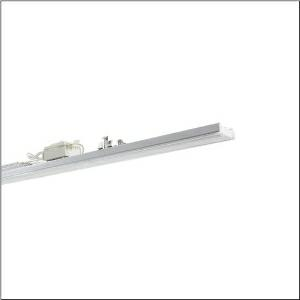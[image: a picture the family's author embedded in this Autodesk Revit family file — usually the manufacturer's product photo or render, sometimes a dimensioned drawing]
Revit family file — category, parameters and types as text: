
# Revit family: licross_r__11_recessed_ho_51te1edv4m5s_c22c
name_source: partatom
category: Lighting Fixtures
units: mm (PartAtom-declared; Revit-internal decimal feet)

## family parameters
Cut with Voids When Loaded = No
Host = Face
Light Source = No
Part Type = Normal
Room Calculation Point = No
Round Connector Dimension = Use Diameter
Shared = No

## types (1)
- --- (1 x LED, 25560 lm, 144.7 W, 4000K)
    Apparent Load = 145 VA
    CIE Flux Codes = 85 95 99 100 100
    Color Rendering = 80
    Color Temperature = 4000K
    Default Elevation = 1800 mm
    Description = Licross® 11 Recessed HO, luminaire insert, of sheet steel, galvanised, coil coated, white, length: 2.250mm, width: 66mm, height: 67mm, LED rated luminous flux: 25.560lm, light colour: 840, control gear: DALI 2, with plug, 5-pole, with phase selection, mains connection: 220..240V, AC, 50/60Hz, rated input power: 145W, internal wiring halogen-free, primary light control with lens, of plastic, primary optical cover: cover, of PMMA, light emission: direct distribution, primary light characteristic: symmetric, protection rating (complete): IP54, insulation class (complete): insulation class I (protective earthing), certification: CE, ENEC, VDE, UKCA, protection symbol: D if used in an environment with non-conductive dust loads with corresponding accessories, impact resistance: IK06, permissible ambient temperature for indoor applications: -40..+35°C, corresponds to IFS (International Featured Standards) requirements for safety and quality in the food industry, reducing of maximum allowable ambient temperature of 5°C with ceiling mounting, LABS conformity tested according to VDMA 24364:2018-05, packaging unit: 1 piece
    Height = 58 mm
    Lamp = 1 x LED
    Lamp Light Flux = 25560 lm
    Lamp Power = 144.7 W
    Lamp count = 1
    Length = 2250 mm
    Luminous efficacy = 177 lm/W
    Manufacturer = Siteco
    ModVariant = No
    Model = 51TE1EDV4M5S
    Mounting Place = Ceiling
    Mounting Type = Pendant
    Number of Poles = 1
    OnlyDefault = Yes
    Power Factor = 1
    Product Name = Licross® 11 Recessed HO
    Product group = luminaire insert | ceiling pendant
    ProductGroupID = 902
    Protection Class = Protection class I
    Protection Degree = IP 54
    RLX_Detail_Level = 1
    RLX_Emergency_Light_Flux = 0 lm
    RLX_Emergency_Type = 0
    RLX_Emergency_Type_DB = No
    RlxData = <blob elided: 29633 chars, md5=eedab52a>
    Socket = socket
    Standby Power = 0 W
    System Light Flux = 25560 lm
    System Power = 145 W
    Type Comments = factory setting: luminous flux: 100 % | dim-lin: 254 | 665 mA
    Type Image = l_1296930.jpg
    URL = http://relux.com
    VarID = @adj_117269
    Voltage = 0 V
    Weight = 0.00 kg
    Width = 66 mm

## geometry (parser evidence)
native form markers: Blend x4, Sweep x11
no freeform markers — native parametric forms only
